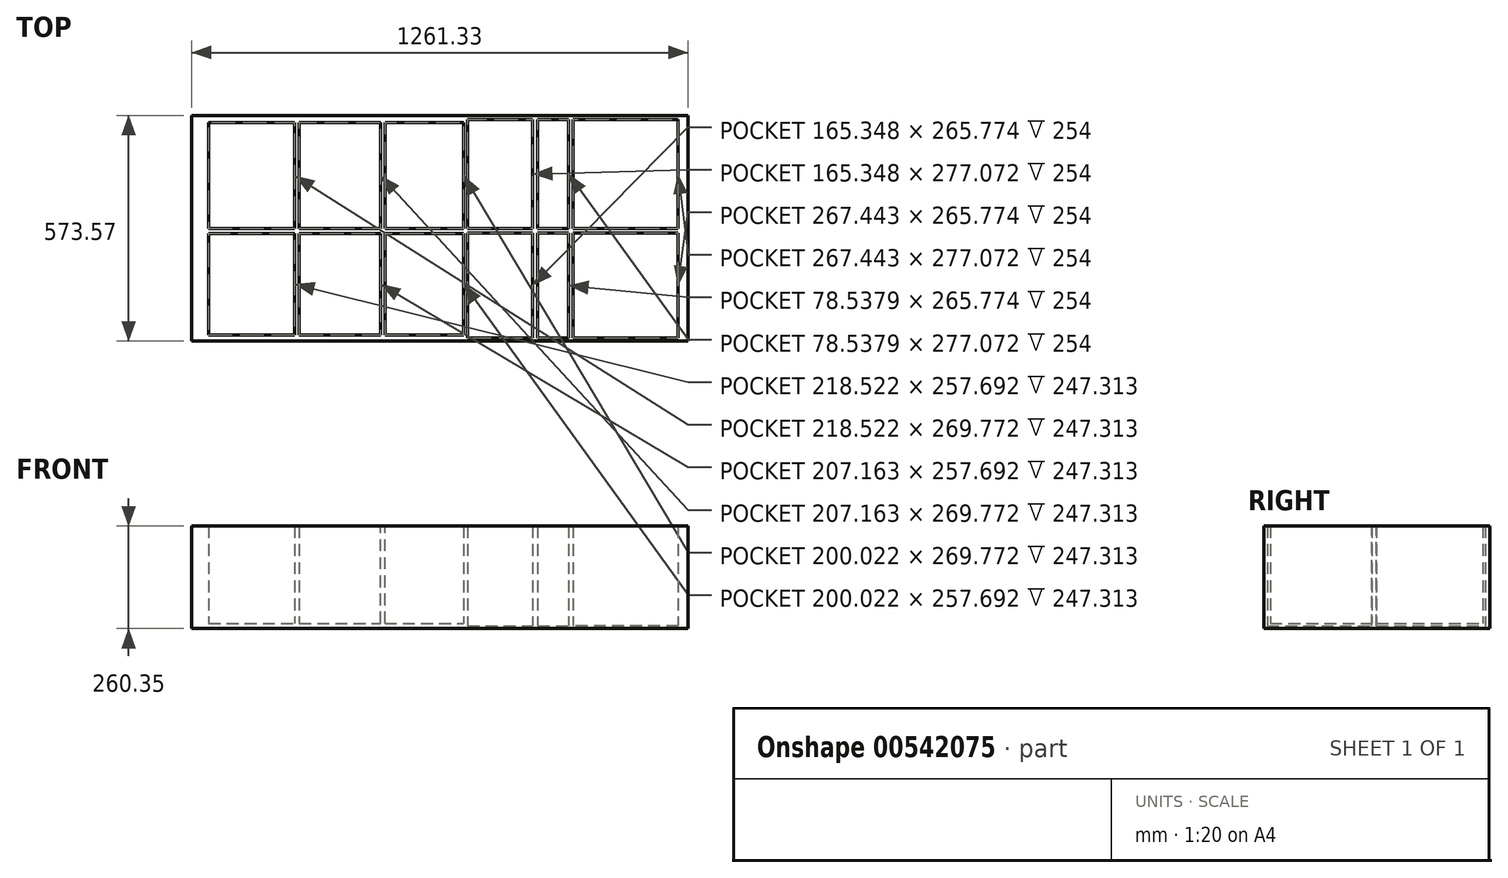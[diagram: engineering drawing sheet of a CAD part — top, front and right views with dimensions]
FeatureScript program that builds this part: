
annotation { "Feature Type Name" : "Feature", "Feature Type Description" : "" }
export const myFeature = defineFeature(function(context is Context, id is Id, definition is map)
    precondition{}
    {
        {
            var Q0;
            Q0=qCreatedBy(makeId("Top.planeOp"),FACE);
            var sketch = newSketch(context, id + "F0", { "sketchPlane" : qUnion([Q0])});
            skLineSegment(sketch, "E0.bottom", {"start": v(200.48, -102.49) * mm, "end": v(-334.4, -102.49) * mm});
            skLineSegment(sketch, "E0.top", {"start": v(200.48, 471.08) * mm, "end": v(-334.4, 471.08) * mm});
            skLineSegment(sketch, "E0.left", {"start": v(200.48, -102.49) * mm, "end": v(200.48, 471.08) * mm});
            skLineSegment(sketch, "E0.right", {"start": v(-334.4, -102.49) * mm, "end": v(-334.4, 471.08) * mm});
            skSolve(sketch);
        }
        {
            var Q0;
            Q0=makeQuery(id+"F0.imprint","IMPRINT",FACE,{"disambiguationData":[TD([[makeQuery(id+"F0.imprint","IMPRINT",EDGE,{"derivedFrom":sQuery(id+"F0.wireOp",EDGE,"E0.bottom")}),-1.0]])]});
            extrude(context, id + "F1", {"entities" : qUnion([Q0]), "depth" : 6.35 * mm, "offsetDistance" : 25.4 * mm});
        }
        {
            var Q0;
            Q0=makeQuery(id+"F1.opExtrude","CAP_FACE",FACE,{"disambiguationData":[OSD([sQuery(id+"F0.wireOp",EDGE,"E0.bottom"),sQuery(id+"F0.wireOp",EDGE,"E0.top"),sQuery(id+"F0.wireOp",EDGE,"E0.left"),sQuery(id+"F0.wireOp",EDGE,"E0.right")])],"isStart":false});
            var sketch = newSketch(context, id + "F2", { "sketchPlane" : qUnion([Q0])});
            skLineSegment(sketch, "E1.bottom", {"start": v(-334.4, -102.49) * mm, "end": v(200.48, -102.49) * mm});
            skLineSegment(sketch, "E1.top", {"start": v(-334.4, -94.2) * mm, "end": v(200.48, -94.2) * mm});
            skLineSegment(sketch, "E1.left", {"start": v(-334.4, -102.49) * mm, "end": v(-334.4, -94.2) * mm});
            skLineSegment(sketch, "E1.right", {"start": v(200.48, -102.49) * mm, "end": v(200.48, -94.2) * mm});
            skSolve(sketch);
        }
        {
            var Q0;
            Q0 = qSketchRegion(id + "F2", true);
            extrude(context, id + "F3", {"entities" : qUnion([Q0]), "operationType" : NewBodyOperationType.ADD, "depth" : 254 * mm, "offsetDistance" : 25.4 * mm});
        }
        {
            var Q0;
            Q0=makeQuery(id+"F1.opExtrude","CAP_FACE",FACE,{"disambiguationData":[OSD([sQuery(id+"F0.wireOp",EDGE,"E0.bottom"),sQuery(id+"F0.wireOp",EDGE,"E0.top"),sQuery(id+"F0.wireOp",EDGE,"E0.left"),sQuery(id+"F0.wireOp",EDGE,"E0.right")])],"isStart":false});
            var sketch = newSketch(context, id + "F4", { "sketchPlane" : qUnion([Q0])});
            skLineSegment(sketch, "E2.bottom", {"start": v(-334.4, 459.95) * mm, "end": v(200.48, 459.95) * mm});
            skLineSegment(sketch, "E2.top", {"start": v(-334.4, 471.08) * mm, "end": v(200.48, 471.08) * mm});
            skLineSegment(sketch, "E2.left", {"start": v(-334.4, 459.95) * mm, "end": v(-334.4, 471.08) * mm});
            skLineSegment(sketch, "E2.right", {"start": v(200.48, 459.95) * mm, "end": v(200.48, 471.08) * mm});
            skSolve(sketch);
        }
        {
            var Q0;
            Q0 = qSketchRegion(id + "F4", true);
            extrude(context, id + "F5", {"entities" : qUnion([Q0]), "operationType" : NewBodyOperationType.ADD, "depth" : 254 * mm, "offsetDistance" : 25.4 * mm});
        }
        {
            var Q0;
            Q0=makeQuery(id+"F1.opExtrude","CAP_FACE",FACE,{"disambiguationData":[OSD([sQuery(id+"F0.wireOp",EDGE,"E0.bottom"),sQuery(id+"F0.wireOp",EDGE,"E0.top"),sQuery(id+"F0.wireOp",EDGE,"E0.left"),sQuery(id+"F0.wireOp",EDGE,"E0.right")])],"isStart":false});
            var sketch = newSketch(context, id + "F6", { "sketchPlane" : qUnion([Q0])});
            skLineSegment(sketch, "E3.bottom", {"start": v(200.48, 182.88) * mm, "end": v(-334.4, 182.88) * mm});
            skLineSegment(sketch, "E3.top", {"start": v(200.48, 171.58) * mm, "end": v(-334.4, 171.58) * mm});
            skLineSegment(sketch, "E3.left", {"start": v(200.48, 182.88) * mm, "end": v(200.48, 171.58) * mm});
            skLineSegment(sketch, "E3.right", {"start": v(-334.4, 182.88) * mm, "end": v(-334.4, 171.58) * mm});
            skSolve(sketch);
        }
        {
            var Q0;
            Q0 = qSketchRegion(id + "F6", true);
            extrude(context, id + "F7", {"entities" : qUnion([Q0]), "operationType" : NewBodyOperationType.ADD, "depth" : 254 * mm, "offsetDistance" : 25.4 * mm});
        }
        {
            var Q0;
            {var subQ0=sQuery(id+"F0.wireOp",EDGE,"E0.right");var subQ1=sQuery(id+"F0.wireOp",EDGE,"E0.left");Q0=makeQuery(id+"F7.boolean.opBoolean","SPLIT",FACE,{"disambiguationData":[TD([makeQuery(id+"F5.opExtrude","SWEPT_FACE",FACE,{"disambiguationData":[OSD([sQuery(id+"F4.wireOp",EDGE,"E2.bottom")])]})])],"derivedFrom":makeQuery(id+"F1.opExtrude","CAP_FACE",FACE,{"disambiguationData":[OSD([sQuery(id+"F0.wireOp",EDGE,"E0.bottom"),sQuery(id+"F0.wireOp",EDGE,"E0.top"),subQ1,subQ0])],"isStart":false})});}
            var sketch = newSketch(context, id + "F8", { "sketchPlane" : qUnion([Q0])});
            skLineSegment(sketch, "E4.bottom", {"start": v(-66.97, 459.95) * mm, "end": v(-77.6, 459.95) * mm});
            skLineSegment(sketch, "E4.top", {"start": v(-66.97, -95.22) * mm, "end": v(-77.6, -95.22) * mm});
            skLineSegment(sketch, "E4.left", {"start": v(-66.97, 459.95) * mm, "end": v(-66.97, -95.22) * mm});
            skLineSegment(sketch, "E4.right", {"start": v(-77.6, 459.95) * mm, "end": v(-77.6, -95.22) * mm});
            skSolve(sketch);
        }
        {
            var Q0;
            Q0 = qSketchRegion(id + "F8", true);
            var Q1;
            {var subQ0=sQuery(id+"F8.wireOp",EDGE,"E4.bottom");Q1=makeQuery(id+"F8.imprint","IMPRINT",FACE,{"disambiguationData":[TD([[makeQuery(id+"F8.imprint","IMPRINT",EDGE,{"derivedFrom":subQ0}),-1.0]])]});}
            extrude(context, id + "F9", {"entities" : qUnion([Q0, Q1]), "operationType" : NewBodyOperationType.ADD, "depth" : 254 * mm, "offsetDistance" : 25.4 * mm});
        }
        {
            var Q0;
            Q0=makeQuery(id+"F7.boolean.opBoolean","MERGE",FACE,{"derivedFrom":[makeQuery(id+"F5.boolean.opBoolean","MERGE",FACE,{"derivedFrom":[makeQuery(id+"F3.boolean.opBoolean","MERGE",FACE,{"derivedFrom":[makeQuery(id+"F1.opExtrude","SWEPT_FACE",FACE,{"disambiguationData":[OSD([sQuery(id+"F0.wireOp",EDGE,"E0.left")])]}),makeQuery(id+"F3.opExtrude","SWEPT_FACE",FACE,{"disambiguationData":[OSD([sQuery(id+"F2.wireOp",EDGE,"E1.right")])]})]}),makeQuery(id+"F5.opExtrude","SWEPT_FACE",FACE,{"disambiguationData":[OSD([sQuery(id+"F4.wireOp",EDGE,"E2.right")])]})]}),makeQuery(id+"F7.opExtrude","SWEPT_FACE",FACE,{"disambiguationData":[OSD([sQuery(id+"F6.wireOp",EDGE,"E3.left")])]})]});
            var sketch = newSketch(context, id + "F10", { "sketchPlane" : qUnion([Q0])});
            skLineSegment(sketch, "E5.bottom", {"start": v(471.08, 0) * mm, "end": v(-102.49, 0) * mm});
            skLineSegment(sketch, "E5.top", {"start": v(471.08, 260.35) * mm, "end": v(-102.49, 260.35) * mm});
            skLineSegment(sketch, "E5.left", {"start": v(471.08, 0) * mm, "end": v(471.08, 260.35) * mm});
            skLineSegment(sketch, "E5.right", {"start": v(-102.49, 0) * mm, "end": v(-102.49, 260.35) * mm});
            skSolve(sketch);
        }
        {
            var Q0;
            Q0 = qSketchRegion(id + "F10", true);
            extrude(context, id + "F11", {"entities" : qUnion([Q0]), "operationType" : NewBodyOperationType.ADD, "depth" : 25.4 * mm, "offsetDistance" : 25.4 * mm});
        }
        {
            var Q0;
            {var subQ1=sQuery(id+"F0.wireOp",EDGE,"E0.right");var subQ4=sQuery(id+"F4.wireOp",EDGE,"E2.bottom");Q0=makeQuery(id+"F9.boolean.opBoolean","SPLIT",FACE,{"disambiguationData":[TD([makeQuery(id+"F1.opExtrude","SWEPT_FACE",FACE,{"disambiguationData":[OSD([subQ1])]})])],"derivedFrom":makeQuery(id+"F5.opExtrude","SWEPT_FACE",FACE,{"disambiguationData":[OSD([subQ4])]})});}
            var sketch = newSketch(context, id + "F12", { "sketchPlane" : qUnion([Q0])});
            skLineSegment(sketch, "E6.bottom", {"start": v(-169.06, 260.35) * mm, "end": v(-156.14, 260.35) * mm});
            skLineSegment(sketch, "E6.top", {"start": v(-169.06, 6.35) * mm, "end": v(-156.14, 6.35) * mm});
            skLineSegment(sketch, "E6.left", {"start": v(-169.06, 260.35) * mm, "end": v(-169.06, 6.35) * mm});
            skLineSegment(sketch, "E6.right", {"start": v(-156.14, 260.35) * mm, "end": v(-156.14, 6.35) * mm});
            skSolve(sketch);
        }
        {
            var Q0;
            Q0 = qSketchRegion(id + "F12", true);
            extrude(context, id + "F13", {"entities" : qUnion([Q0]), "operationType" : NewBodyOperationType.ADD, "depth" : 558.8 * mm, "offsetDistance" : 25.4 * mm});
        }
        {
            var Q0;
            Q0=makeQuery(id+"F7.boolean.opBoolean","MERGE",FACE,{"derivedFrom":[makeQuery(id+"F5.boolean.opBoolean","MERGE",FACE,{"derivedFrom":[makeQuery(id+"F3.boolean.opBoolean","MERGE",FACE,{"derivedFrom":[makeQuery(id+"F1.opExtrude","SWEPT_FACE",FACE,{"disambiguationData":[OSD([sQuery(id+"F0.wireOp",EDGE,"E0.right")])]}),makeQuery(id+"F3.opExtrude","SWEPT_FACE",FACE,{"disambiguationData":[OSD([sQuery(id+"F2.wireOp",EDGE,"E1.left")])]})]}),makeQuery(id+"F5.opExtrude","SWEPT_FACE",FACE,{"disambiguationData":[OSD([sQuery(id+"F4.wireOp",EDGE,"E2.left")])]})]}),makeQuery(id+"F7.opExtrude","SWEPT_FACE",FACE,{"disambiguationData":[OSD([sQuery(id+"F6.wireOp",EDGE,"E3.right")])]})]});
            var sketch = newSketch(context, id + "F14", { "sketchPlane" : qUnion([Q0])});
            skLineSegment(sketch, "E7.bottom", {"start": v(-471.08, 260.35) * mm, "end": v(102.49, 260.35) * mm});
            skLineSegment(sketch, "E7.top", {"start": v(-471.08, 0) * mm, "end": v(102.49, 0) * mm});
            skLineSegment(sketch, "E7.left", {"start": v(-471.08, 260.35) * mm, "end": v(-471.08, 0) * mm});
            skLineSegment(sketch, "E7.right", {"start": v(102.49, 260.35) * mm, "end": v(102.49, 0) * mm});
            skSolve(sketch);
        }
        {
            var Q0;
            Q0 = qSketchRegion(id + "F14", true);
            extrude(context, id + "F15", {"entities" : qUnion([Q0]), "operationType" : NewBodyOperationType.ADD, "depth" : 10.16 * mm, "offsetDistance" : 25.4 * mm});
        }
        {
            var Q0;
            Q0=makeQuery(id+"F15.opExtrude","CAP_FACE",FACE,{"disambiguationData":[OSD([sQuery(id+"F14.wireOp",EDGE,"E7.bottom"),sQuery(id+"F14.wireOp",EDGE,"E7.top"),sQuery(id+"F14.wireOp",EDGE,"E7.left"),sQuery(id+"F14.wireOp",EDGE,"E7.right")])],"isStart":false});
            var sketch = newSketch(context, id + "F16", { "sketchPlane" : qUnion([Q0])});
            skLineSegment(sketch, "E8.bottom", {"start": v(102.49, 260.35) * mm, "end": v(86.69, 260.35) * mm});
            skLineSegment(sketch, "E8.top", {"start": v(102.49, 0) * mm, "end": v(86.69, 0) * mm});
            skLineSegment(sketch, "E8.left", {"start": v(102.49, 260.35) * mm, "end": v(102.49, 0) * mm});
            skLineSegment(sketch, "E8.right", {"start": v(86.69, 260.35) * mm, "end": v(86.69, 0) * mm});
            skSolve(sketch);
        }
        {
            var Q0;
            Q0 = qSketchRegion(id + "F16", true);
            extrude(context, id + "F17", {"entities" : qUnion([Q0]), "operationType" : NewBodyOperationType.ADD, "depth" : 690.88 * mm, "offsetDistance" : 25.4 * mm});
        }
        {
            var Q0;
            Q0=makeQuery(id+"F15.opExtrude","CAP_FACE",FACE,{"disambiguationData":[OSD([sQuery(id+"F14.wireOp",EDGE,"E7.bottom"),sQuery(id+"F14.wireOp",EDGE,"E7.top"),sQuery(id+"F14.wireOp",EDGE,"E7.left"),sQuery(id+"F14.wireOp",EDGE,"E7.right")])],"isStart":false});
            var sketch = newSketch(context, id + "F18", { "sketchPlane" : qUnion([Q0])});
            skLineSegment(sketch, "E9.bottom", {"start": v(-471.08, 260.35) * mm, "end": v(-452.86, 260.35) * mm});
            skLineSegment(sketch, "E9.top", {"start": v(-471.08, 0) * mm, "end": v(-452.86, 0) * mm});
            skLineSegment(sketch, "E9.left", {"start": v(-471.08, 260.35) * mm, "end": v(-471.08, 0) * mm});
            skLineSegment(sketch, "E9.right", {"start": v(-452.86, 260.35) * mm, "end": v(-452.86, 0) * mm});
            skSolve(sketch);
        }
        {
            var Q0;
            Q0 = qSketchRegion(id + "F18", true);
            extrude(context, id + "F19", {"entities" : qUnion([Q0]), "operationType" : NewBodyOperationType.ADD, "depth" : 690.88 * mm, "offsetDistance" : 25.4 * mm});
        }
        {
            var Q0;
            Q0=makeQuery(id+"F15.opExtrude","CAP_FACE",FACE,{"disambiguationData":[OSD([sQuery(id+"F14.wireOp",EDGE,"E7.bottom"),sQuery(id+"F14.wireOp",EDGE,"E7.top"),sQuery(id+"F14.wireOp",EDGE,"E7.left"),sQuery(id+"F14.wireOp",EDGE,"E7.right")])],"isStart":false});
            var sketch = newSketch(context, id + "F20", { "sketchPlane" : qUnion([Q0])});
            skLineSegment(sketch, "E10.bottom", {"start": v(-183.09, 260.35) * mm, "end": v(-171, 260.35) * mm});
            skLineSegment(sketch, "E10.top", {"start": v(-183.09, 0) * mm, "end": v(-171, 0) * mm});
            skLineSegment(sketch, "E10.left", {"start": v(-183.09, 260.35) * mm, "end": v(-183.09, 0) * mm});
            skLineSegment(sketch, "E10.right", {"start": v(-171, 260.35) * mm, "end": v(-171, 0) * mm});
            skSolve(sketch);
        }
        {
            var Q0;
            Q0 = qSketchRegion(id + "F20", true);
            extrude(context, id + "F21", {"entities" : qUnion([Q0]), "operationType" : NewBodyOperationType.ADD, "depth" : 690.88 * mm, "offsetDistance" : 25.4 * mm});
        }
        {
            var Q0;
            Q0=makeQuery(id+"F19.opExtrude","SWEPT_FACE",FACE,{"disambiguationData":[OSD([sQuery(id+"F18.wireOp",EDGE,"E9.right")])]});
            var sketch = newSketch(context, id + "F22", { "sketchPlane" : qUnion([Q0])});
            skLineSegment(sketch, "E11.bottom", {"start": v(-554.78, 260.35) * mm, "end": v(-544.6, 260.35) * mm});
            skLineSegment(sketch, "E11.top", {"start": v(-554.78, 0) * mm, "end": v(-544.6, 0) * mm});
            skLineSegment(sketch, "E11.left", {"start": v(-554.78, 260.35) * mm, "end": v(-554.78, 0) * mm});
            skLineSegment(sketch, "E11.right", {"start": v(-544.6, 260.35) * mm, "end": v(-544.6, 0) * mm});
            skSolve(sketch);
        }
        {
            var Q0;
            Q0 = qSketchRegion(id + "F22", true);
            extrude(context, id + "F23", {"entities" : qUnion([Q0]), "operationType" : NewBodyOperationType.ADD, "depth" : 553.72 * mm, "offsetDistance" : 25.4 * mm});
        }
        {
            var Q0;
            {var subQ2=sQuery(id+"F16.wireOp",EDGE,"E8.right");Q0=makeQuery(id+"F23.boolean.opBoolean","SPLIT",FACE,{"disambiguationData":[TD([makeQuery(id+"F23.opExtrude","SWEPT_FACE",FACE,{"disambiguationData":[OSD([sQuery(id+"F22.wireOp",EDGE,"E11.left")])]})])],"derivedFrom":makeQuery(id+"F17.opExtrude","SWEPT_FACE",FACE,{"disambiguationData":[OSD([subQ2])]})});}
            var sketch = newSketch(context, id + "F24", { "sketchPlane" : qUnion([Q0])});
            skLineSegment(sketch, "E12.bottom", {"start": v(773.75, 260.35) * mm, "end": v(761.95, 260.35) * mm});
            skLineSegment(sketch, "E12.top", {"start": v(773.75, 0) * mm, "end": v(761.95, 0) * mm});
            skLineSegment(sketch, "E12.left", {"start": v(773.75, 260.35) * mm, "end": v(773.75, 0) * mm});
            skLineSegment(sketch, "E12.right", {"start": v(761.95, 260.35) * mm, "end": v(761.95, 0) * mm});
            skSolve(sketch);
        }
        {
            var Q0;
            Q0 = qSketchRegion(id + "F24", true);
            extrude(context, id + "F25", {"entities" : qUnion([Q0]), "operationType" : NewBodyOperationType.ADD, "depth" : 551.18 * mm, "offsetDistance" : 25.4 * mm});
        }
        {
            var Q0;
            Q0=makeQuery(id+"F17.opExtrude","CAP_FACE",FACE,{"disambiguationData":[OSD([sQuery(id+"F16.wireOp",EDGE,"E8.bottom"),sQuery(id+"F16.wireOp",EDGE,"E8.top"),sQuery(id+"F16.wireOp",EDGE,"E8.left"),sQuery(id+"F16.wireOp",EDGE,"E8.right")])],"isStart":false});
            var sketch = newSketch(context, id + "F26", { "sketchPlane" : qUnion([Q0])});
            skLineSegment(sketch, "E13.bottom", {"start": v(102.49, 260.35) * mm, "end": v(-469.15, 260.35) * mm});
            skLineSegment(sketch, "E13.top", {"start": v(102.49, 0) * mm, "end": v(-469.15, 0) * mm});
            skLineSegment(sketch, "E13.left", {"start": v(102.49, 260.35) * mm, "end": v(102.49, 0) * mm});
            skLineSegment(sketch, "E13.right", {"start": v(-469.15, 260.35) * mm, "end": v(-469.15, 0) * mm});
            skSolve(sketch);
        }
        {
            var Q0;
            Q0 = qSketchRegion(id + "F26", true);
            extrude(context, id + "F27", {"entities" : qUnion([Q0]), "operationType" : NewBodyOperationType.ADD, "oppositeDirection" : true, "depth" : 43.18 * mm, "offsetDistance" : 25.4 * mm});
        }
        {
            var Q0;
            {var subQ0=sQuery(id+"F14.wireOp",EDGE,"E7.bottom");var subQ1=sQuery(id+"F14.wireOp",EDGE,"E7.top");Q0=makeQuery(id+"F21.boolean.opBoolean","SPLIT",FACE,{"disambiguationData":[TD([makeQuery(id+"F17.opExtrude","SWEPT_FACE",FACE,{"disambiguationData":[OSD([sQuery(id+"F16.wireOp",EDGE,"E8.right")])]})])],"derivedFrom":makeQuery(id+"F15.opExtrude","CAP_FACE",FACE,{"disambiguationData":[OSD([subQ0,subQ1,sQuery(id+"F14.wireOp",EDGE,"E7.left"),sQuery(id+"F14.wireOp",EDGE,"E7.right")])],"isStart":false})});}
            var sketch = newSketch(context, id + "F28", { "sketchPlane" : qUnion([Q0])});
            skLineSegment(sketch, "E14.bottom", {"start": v(86.69, 0) * mm, "end": v(-461.2, 0) * mm});
            skLineSegment(sketch, "E14.top", {"start": v(86.69, 13.04) * mm, "end": v(-461.2, 13.04) * mm});
            skLineSegment(sketch, "E14.left", {"start": v(86.69, 0) * mm, "end": v(86.69, 13.04) * mm});
            skLineSegment(sketch, "E14.right", {"start": v(-461.2, 0) * mm, "end": v(-461.2, 13.04) * mm});
            skSolve(sketch);
        }
        {
            var Q0;
            Q0 = qSketchRegion(id + "F28", true);
            extrude(context, id + "F29", {"entities" : qUnion([Q0]), "operationType" : NewBodyOperationType.ADD, "depth" : 688.34 * mm, "offsetDistance" : 25.4 * mm});
        }
    });
